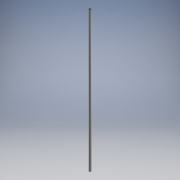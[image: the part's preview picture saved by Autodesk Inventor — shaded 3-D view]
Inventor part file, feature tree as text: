
AUTODESK INVENTOR PART (.ipt)
format: ipt  version: 2018 (Build 220112000, 112)  size: 93,696 bytes
history: native  units: mm
features: other x1, extrude x1, sketch x1
ambient origin geometry x8: Origin, YZ Plane, XZ Plane, XY Plane, X Axis, Y Axis, Z Axis, Center Point
bodies: Body1 (feature_tree)
feature tree (3):
  other  "ソリッド1"
  extrude  "押し出し1"  Depth=2.0mm
  sketch  "スケッチ1"
